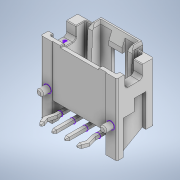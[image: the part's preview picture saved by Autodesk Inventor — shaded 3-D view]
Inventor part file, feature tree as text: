
AUTODESK INVENTOR PART (.ipt)
format: ipt  version: 2022 (Build 260153000, 153)  size: 343,552 bytes
history: native  units: in
note: dims shown in document units (in); Inventor stores cm internally (conversion verified against a paired STEP export)
features: sketch x2, other x1, extrude x1, imported_body x1
ambient origin geometry x8: Origin, YZ Plane, XZ Plane, XY Plane, X Axis, Y Axis, Z Axis, Center Point
bodies: Solid1 (feature_tree)
feature tree (5):
  other  "Repaired Geometry1"
  extrude  "Extrusion1"  [1 undecoded]
  sketch  "3D Sketch1"
  sketch  "Sketch1"  dims[d0=0.0039in d1=0.0in]
  imported_body  "Base1"
note: 1 required parameter value undecoded (feature->parameter linkage not recoverable at this tier; creation-order binding heuristic only, values carry confidence <= 0.55)
